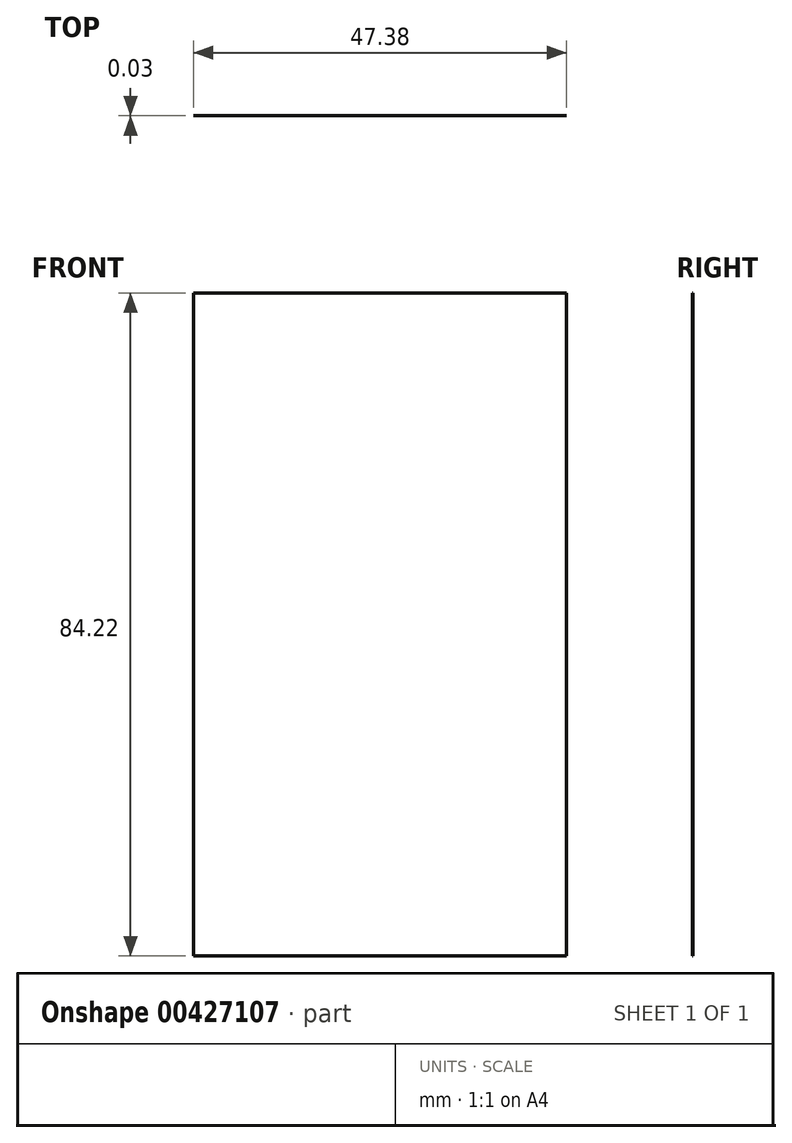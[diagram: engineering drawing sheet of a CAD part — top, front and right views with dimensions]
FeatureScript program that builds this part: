
annotation { "Feature Type Name" : "Feature", "Feature Type Description" : "" }
export const myFeature = defineFeature(function(context is Context, id is Id, definition is map)
    precondition{}
    {
        {
            var Q0;
            Q0=qCreatedBy(makeId("Front.planeOp"),FACE);
            var sketch = newSketch(context, id + "F0", { "sketchPlane" : qUnion([Q0])});
            skLineSegment(sketch, "E0.bottom", {"start": v(23.7, 42.11) * mm, "end": v(-23.7, 42.11) * mm});
            skLineSegment(sketch, "E0.top", {"start": v(23.7, -42.11) * mm, "end": v(-23.7, -42.11) * mm});
            skLineSegment(sketch, "E0.left", {"start": v(23.7, 42.11) * mm, "end": v(23.7, -42.11) * mm});
            skLineSegment(sketch, "E0.right", {"start": v(-23.7, 42.11) * mm, "end": v(-23.7, -42.11) * mm});
            skSolve(sketch);
        }
        {
            var Q0;
            Q0=makeQuery(id+"F0.imprint","IMPRINT",FACE,{"disambiguationData":[TD([[makeQuery(id+"F0.imprint","IMPRINT",EDGE,{"derivedFrom":sQuery(id+"F0.wireOp",EDGE,"E0.bottom")}),1.0]])]});
            extrude(context, id + "F1", {"entities" : qUnion([Q0]), "depth" : 0.03 * mm});
        }
    });
